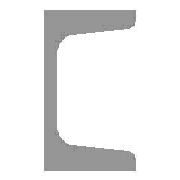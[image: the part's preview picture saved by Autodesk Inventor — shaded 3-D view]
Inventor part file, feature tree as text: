
AUTODESK INVENTOR PART (.ipt)
format: ipt  version: 2017 (Build 210142000, 142)  size: 146,432 bytes
history: native  units: mm (DEFAULTED — no unit token found)
features: other x4, plane x3, split x2, sketch x2
ambient origin geometry x8: Origin, YZ Plane, XZ Plane, XY Plane, X Axis, Y Axis, Z Axis, Center Point
bodies: Solid1 (feature_tree), Body (feature_tree)
feature tree (11):
  parser-record x1  (decoder bookkeeping rows leaked as tree rows — omitted from the tree; the rows remain in map.json)
  other  "Driven Length"
  other  "Start plane"
  other  "End plane"
  plane  "Work Plane4"
  split  "Split1"
  plane  "Work Plane5"
  split  "Split2"
  sketch  "Sketch3"  dims[d0=4.6736mm]
  plane  "Work Plane3"
  sketch  "Sketch4"  dims[d1=50.8mm d2=40.2336mm d3=7.5184mm d4=17.682845mm d5=0.926581mm d6=1219.2mm d7=0.0mm d25=0.0mm d26=-0.0mm d27=1219.2mm d28=6.712646mm d29=2.2352mm d30=90.0deg d31=1219.2mm]
